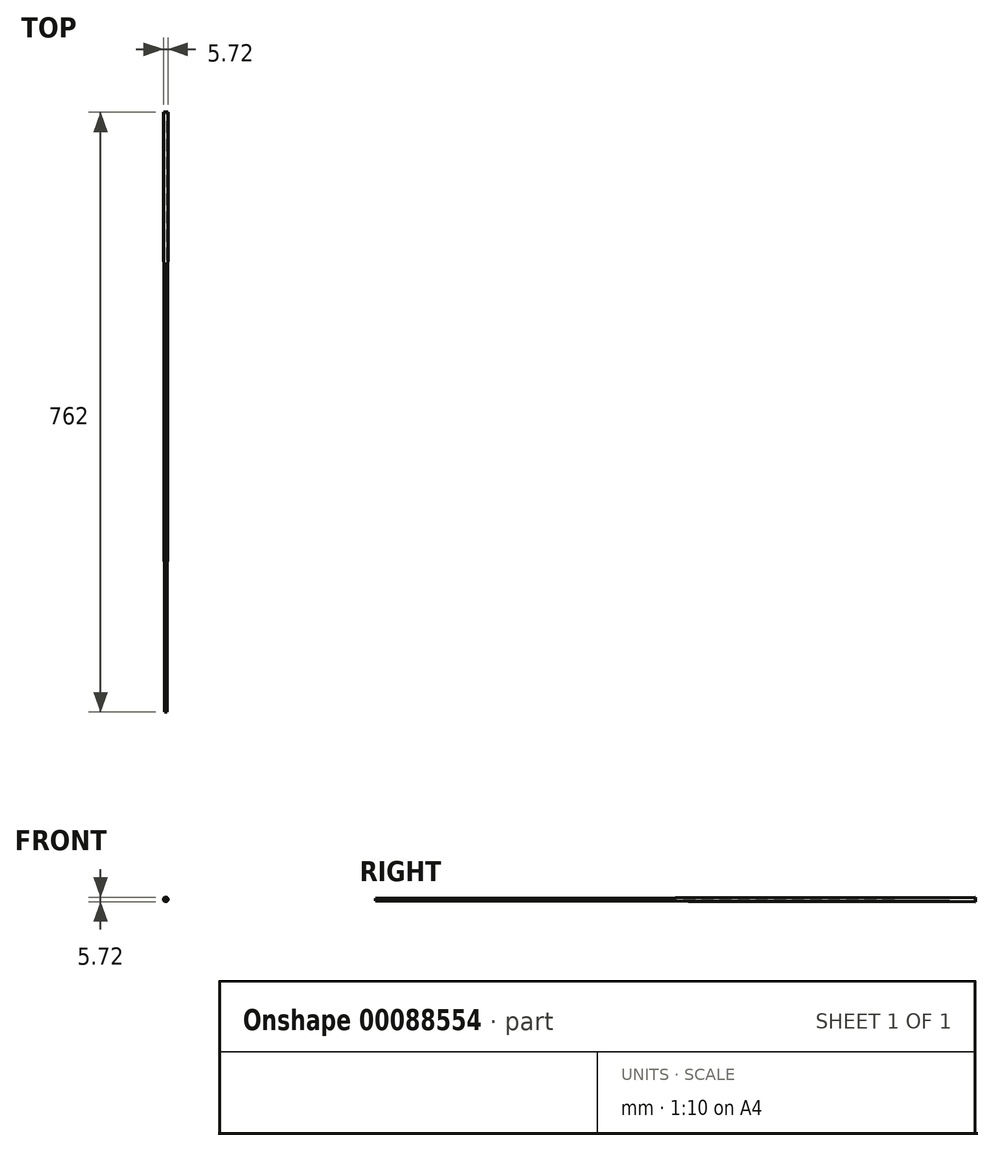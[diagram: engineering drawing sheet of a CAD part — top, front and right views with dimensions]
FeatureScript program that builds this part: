
annotation { "Feature Type Name" : "Feature", "Feature Type Description" : "" }
export const myFeature = defineFeature(function(context is Context, id is Id, definition is map)
    precondition{}
    {
        {
            var Q0;
            Q0=qCreatedBy(makeId("Front.planeOp"),FACE);
            var sketch = newSketch(context, id + "F0", { "sketchPlane" : qUnion([Q0])});
            skCircle(sketch, "E0", {"center": v(0, 0) * mm, "radius": 3.18 * mm});
            skCircle(sketch, "E1", {"center": v(0, 0) * mm, "radius": 2.86 * mm});
            skSolve(sketch);
        }
        {
            var Q0;
            Q0=qCreatedBy(makeId("Front.planeOp"),FACE);
            cPlane(context, id + "F1", {"entities" : qUnion([Q0]), "cplaneType" : CPlaneType.OFFSET, "offset" : 762 * mm, "width" : 152.4 * mm, "height" : 152.4 * mm});
        }
        {
            var Q0;
            Q0=qCreatedBy(id+"F1.planeOp",FACE);
            var sketch = newSketch(context, id + "F2", { "sketchPlane" : qUnion([Q0])});
            skCircle(sketch, "E2", {"center": v(0, 0) * mm, "radius": 1.9 * mm});
            skCircle(sketch, "E3", {"center": v(0, 0) * mm, "radius": 1.59 * mm});
            skSolve(sketch);
        }
        {
            var Q0;
            Q0=makeQuery(id+"F2.imprint","IMPRINT",FACE,{"disambiguationData":[TD([[makeQuery(id+"F2.imprint","IMPRINT",EDGE,{"derivedFrom":sQuery(id+"F2.wireOp",EDGE,"E3")}),1.0]])]});
            var Q1;
            Q1=makeQuery(id+"F0.imprint","IMPRINT",FACE,{"disambiguationData":[TD([[makeQuery(id+"F0.imprint","IMPRINT",EDGE,{"derivedFrom":sQuery(id+"F0.wireOp",EDGE,"E1")}),1.0]])]});
            loft(context, id + "F3", {"sheetProfilesArray" : [{ "sheetProfileEntities" : qUnion([Q0]) }, { "sheetProfileEntities" : qUnion([Q1]) }]});
        }
        {
            var Q0;
            Q0=makeQuery(id+"F3.opLoft","CAP_FACE",FACE,{"disambiguationData":[OSD([makeQuery(id+"F2.imprint","IMPRINT",FACE,{"disambiguationData":[TD([[makeQuery(id+"F2.imprint","IMPRINT",EDGE,{"derivedFrom":sQuery(id+"F2.wireOp",EDGE,"E3")}),1.0]])]})])],"isStart":true});
            var sketch = newSketch(context, id + "F4", { "sketchPlane" : qUnion([Q0])});
            skCircle(sketch, "E4", {"center": v(0, 0) * mm, "radius": 0.67 * mm});
            skSolve(sketch);
        }
        {
            var Q0;
            Q0=makeQuery(id+"F3.opLoft","CAP_FACE",FACE,{"disambiguationData":[OSD([makeQuery(id+"F0.imprint","IMPRINT",FACE,{"disambiguationData":[TD([[makeQuery(id+"F0.imprint","IMPRINT",EDGE,{"derivedFrom":sQuery(id+"F0.wireOp",EDGE,"E1")}),1.0]])]})])],"isStart":true});
            var sketch = newSketch(context, id + "F5", { "sketchPlane" : qUnion([Q0])});
            skCircle(sketch, "E5", {"center": v(0, 0) * mm, "radius": 1.7 * mm});
            skSolve(sketch);
        }
        {
            var Q1;
            Q1=makeQuery(id+"F5.imprint","IMPRINT",FACE,{"disambiguationData":[TD([[makeQuery(id+"F5.imprint","IMPRINT",EDGE,{"derivedFrom":sQuery(id+"F5.wireOp",EDGE,"E5")}),1.0]])]});
            var Q2;
            Q2=makeQuery(id+"F4.imprint","IMPRINT",FACE,{"disambiguationData":[TD([[makeQuery(id+"F4.imprint","IMPRINT",EDGE,{"derivedFrom":sQuery(id+"F4.wireOp",EDGE,"E4")}),1.0]])]});
            loft(context, id + "F6", {"operationType" : NewBodyOperationType.REMOVE, "sheetProfilesArray" : [{ "sheetProfileEntities" : qUnion([Q1]) }, { "sheetProfileEntities" : qUnion([Q2]) }]});
        }
    });
